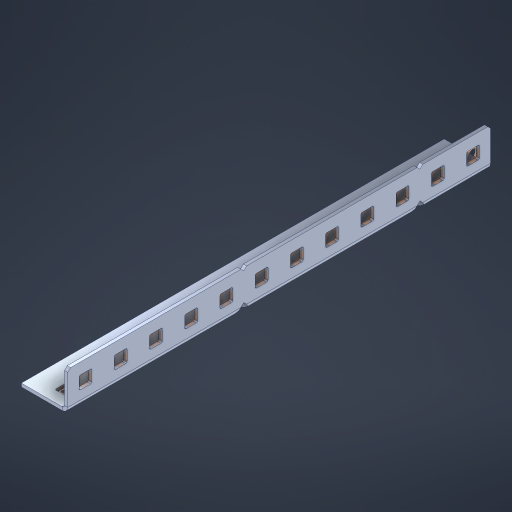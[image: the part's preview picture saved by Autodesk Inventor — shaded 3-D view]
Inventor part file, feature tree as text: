
AUTODESK INVENTOR PART (.ipt)
format: ipt  version: 2023 (Build 270158000, 158)  size: 603,648 bytes
history: native  units: in
note: dims shown in document units (in); Inventor stores cm internally (conversion verified against a paired STEP export)
features: other x29, extrude x23, sheet_metal_op x10, sketch x8, mirror x1, pattern_linear x1, chamfer x1
ambient origin geometry x8: Origin, YZ Plane, XZ Plane, XY Plane, X Axis, Y Axis, Z Axis, Center Point
bodies: Solid1 (feature_tree), Body (feature_tree)
feature tree (73):
  other  "Flange Pattern Plane"
  sheet_metal_op  "Flange Pattern"
  sheet_metal_op  "Body Pattern"
  other  "Arc Length"
  mirror  "Notch Mirror"
  pattern_linear  "Notch Pattern"  Spacing1=0.1875in  [1 undecoded]
  chamfer  "End Chamfer"
  extrude  "Half Cut"  Depth=0.0469in
  sketch  "Sketch1"  dims[d0=2.5in]
  other  "Plate1"
  sketch  "Sketch2"  dims[d1=6.0in]
  other  "Plate2"
  sheet_metal_op  "Bend1"
  sheet_metal_op  "Corner1"
  sketch  "Sketch3"  dims[d2=0.0469in]
  other  "Flange Pattern Sketch"
  sketch  "Sketch7"  dims[d3=0.0469in]
  other  "Srf1"
  other  "Srf2"
  sketch  "Sketch8"  dims[d4=0.0234in]
  sketch  "Sketch9"  dims[d5=0.0938in]
  other  "Srf91"
  sheet_metal_op  "Body Pattern Sketch"
  other  "Srf92"
  sketch  "Sketch13"  dims[d6=0.0469in]
  sketch  "Sketch14"  dims[d7=0.5in d8=90.0deg d9=0.0312in d10=0.1875in d11=0.0469in d12=0.0469in d16=0.182in d17=0.02in d18=0.0469in d19=0.0in d20=0.25in d21=0.25in d46=0.172in d47=1.0in d48=0.0in d49=0.182in d50=0.02in d51=0.25in d52=0.25in d53=0.0469in d54=0.0in d55=0.172in d56=1.0in d57=0.0in d60=4.7244in d62=0.5in d63=0.3937in d65=0.5in d85=0.1227in d86=0.1659in d88=0.04in d89=0.0469in d90=0.0in d91=0.04in d92=0.0491in d95=2.5in d96=0.04in d97=0.25in d98=45.0deg d101=0.0in d102=2.497in d131=0.5in d132=4.7244in d134=0.5in d139=0.5in]
  other  "Srf856"
  other  "Srf1310"
  other  "Srf1311"
  other  "Srf1312"
  other  "Srf1376"
  other  "Srf1377"
  other  "Srf1728"
  other  "Srf1755"
  other  "Srf1878"
  other  "Srf1879"
  other  "Srf1880"
  other  "Srf1881"
  other  "Srf1882"
  other  "Srf1883"
  other  "Srf1942"
  other  "Srf1943"
  other  "Srf1944"
  other  "Srf1945"
  other  "Srf1946"
  other  "Srf1947"
  sheet_metal_op  "Flange Stamp"
  sheet_metal_op  "Flange Circle"
  sheet_metal_op  "Body Stamp"
  sheet_metal_op  "Body Circle"
  sheet_metal_op  "Notch"
  extrude  "ExtrusionSrf2"  Depth=0.0469in
  extrude  "ExtrusionSrf92"  Depth=0.5in
  extrude  "ExtrusionSrf856"  Depth=0.02in
  extrude  "ExtrusionSrf1310"  Depth=0.0469in
  extrude  "ExtrusionSrf1311"  TaperAngle=0.0deg  [1 undecoded]
  extrude  "ExtrusionSrf1312"  Depth=0.5in
  extrude  "ExtrusionSrf1376"  Depth=0.5in
  extrude  "ExtrusionSrf1377"  Depth=0.5in
  extrude  "ExtrusionSrf1728"  Depth=0.5in TaperAngle=0.0deg
  extrude  "ExtrusionSrf1755"  Depth=0.5in
  extrude  "ExtrusionSrf1878"  Depth=0.02in
  extrude  "ExtrusionSrf1879"  Depth=0.5in
  extrude  "ExtrusionSrf1880"  Depth=0.5in
  extrude  "ExtrusionSrf1881"  Depth=0.0469in
  extrude  "ExtrusionSrf1882"  TaperAngle=0.0deg  [1 undecoded]
  extrude  "ExtrusionSrf1883"  Depth=0.5in
  extrude  "ExtrusionSrf1942"  Depth=0.5in TaperAngle=0.0deg
  extrude  "ExtrusionSrf1943"  Depth=0.5in
  extrude  "ExtrusionSrf1944"  Depth=0.5in
  extrude  "ExtrusionSrf1945"  Depth=0.5in
  extrude  "ExtrusionSrf1946"  Depth=0.5in
  extrude  "ExtrusionSrf1947"  Depth=0.5in
note: 3 required parameter values undecoded (feature->parameter linkage not recoverable at this tier; creation-order binding heuristic only, values carry confidence <= 0.55)
